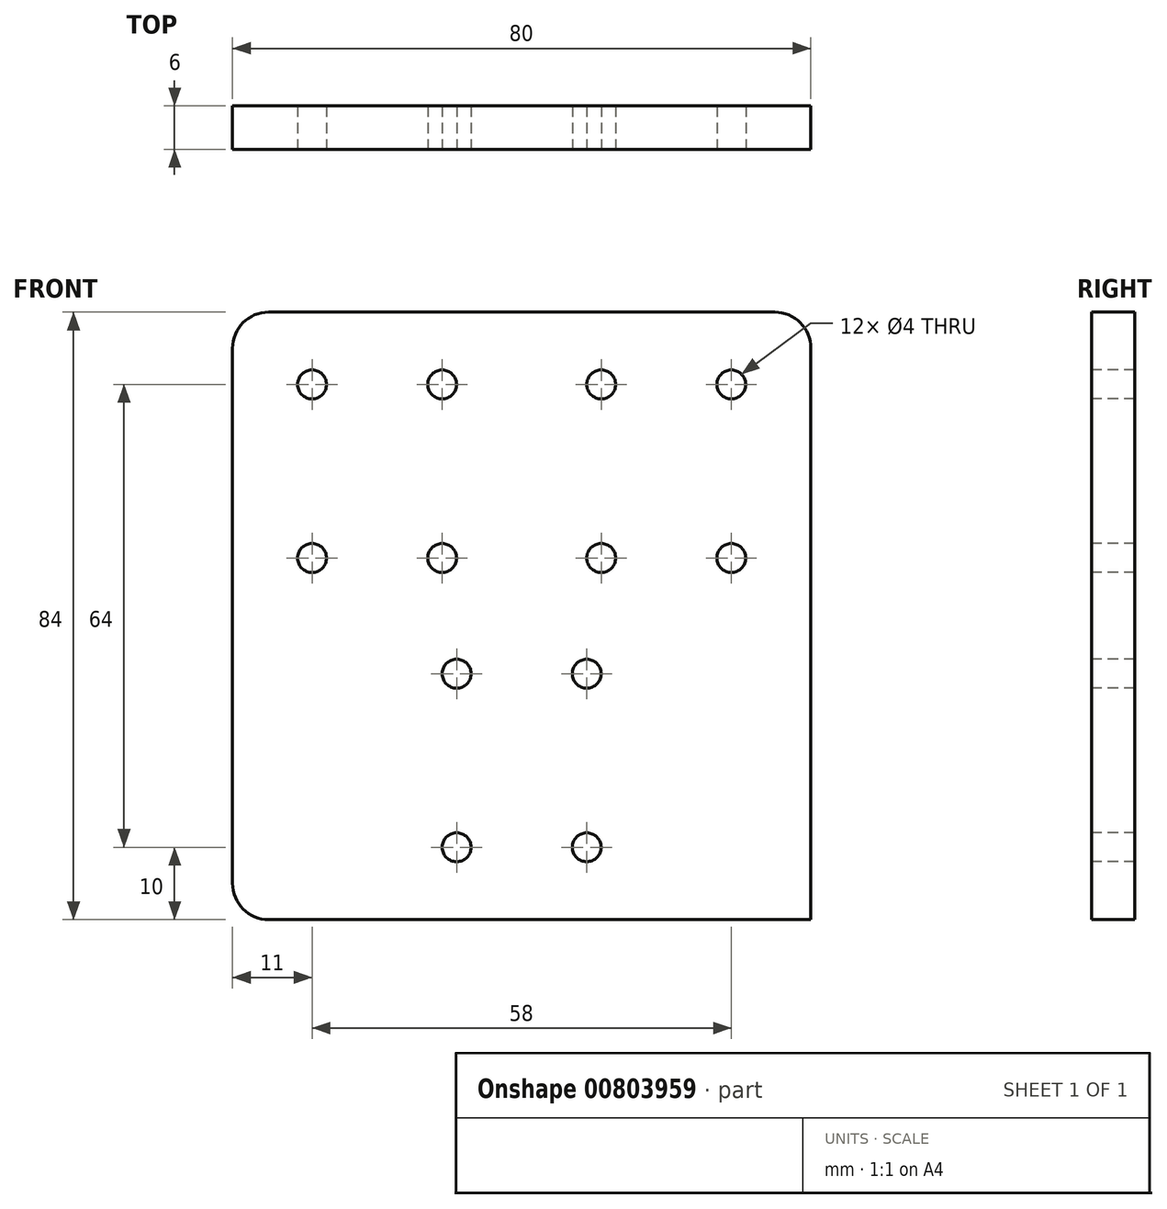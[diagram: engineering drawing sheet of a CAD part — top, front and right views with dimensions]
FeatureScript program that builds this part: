
annotation { "Feature Type Name" : "Feature", "Feature Type Description" : "" }
export const myFeature = defineFeature(function(context is Context, id is Id, definition is map)
    precondition{}
    {
        {
            var Q0;
            Q0=qCreatedBy(makeId("Front.planeOp"),FACE);
            var sketch = newSketch(context, id + "F0", { "sketchPlane" : qUnion([Q0])});
            skLineSegment(sketch, "E0.bottom", {"start": v(40, 42) * mm, "end": v(-40, 42) * mm});
            skLineSegment(sketch, "E0.top", {"start": v(40, -42) * mm, "end": v(-40, -42) * mm});
            skLineSegment(sketch, "E0.left", {"start": v(40, 42) * mm, "end": v(40, -42) * mm});
            skLineSegment(sketch, "E0.right", {"start": v(-40, 42) * mm, "end": v(-40, -42) * mm});
            skPoint(sketch, "E0.middle", {"position": v(0, 0) * mm});
            skLineSegment(sketch, "E1.bottom", {"start": v(5, 37) * mm, "end": v(35, 37) * mm});
            skLineSegment(sketch, "E1.top", {"start": v(5, 3) * mm, "end": v(35, 3) * mm});
            skLineSegment(sketch, "E1.left", {"start": v(5, 37) * mm, "end": v(5, 3) * mm});
            skLineSegment(sketch, "E1.right", {"start": v(35, 37) * mm, "end": v(35, 3) * mm});
            skLineSegment(sketch, "E2.bottom", {"start": v(-35, 37) * mm, "end": v(-5, 37) * mm});
            skLineSegment(sketch, "E2.top", {"start": v(-35, 3) * mm, "end": v(-5, 3) * mm});
            skLineSegment(sketch, "E2.left", {"start": v(-35, 37) * mm, "end": v(-35, 3) * mm});
            skLineSegment(sketch, "E2.right", {"start": v(-5, 37) * mm, "end": v(-5, 3) * mm});
            skLineSegment(sketch, "E3.bottom", {"start": v(-15, -3) * mm, "end": v(15, -3) * mm});
            skLineSegment(sketch, "E3.top", {"start": v(-15, -37) * mm, "end": v(15, -37) * mm});
            skLineSegment(sketch, "E3.left", {"start": v(-15, -3) * mm, "end": v(-15, -37) * mm});
            skLineSegment(sketch, "E3.right", {"start": v(15, -3) * mm, "end": v(15, -37) * mm});
            skPoint(sketch, "E4", {"position": v(0, -20) * mm});
            skLineSegment(sketch, "E5.bottom", {"start": v(9, -8) * mm, "end": v(-9, -8) * mm});
            skLineSegment(sketch, "E5.top", {"start": v(9, -32) * mm, "end": v(-9, -32) * mm});
            skLineSegment(sketch, "E5.left", {"start": v(9, -8) * mm, "end": v(9, -32) * mm});
            skLineSegment(sketch, "E5.right", {"start": v(-9, -8) * mm, "end": v(-9, -32) * mm});
            skPoint(sketch, "E6", {"position": v(20, 20) * mm});
            skPoint(sketch, "E6.positionSnap0", {"position": v(20, 3) * mm});
            skPoint(sketch, "E7", {"position": v(-20, 20) * mm});
            skLineSegment(sketch, "E8.bottom", {"start": v(29, 32) * mm, "end": v(11, 32) * mm});
            skLineSegment(sketch, "E8.top", {"start": v(29, 8) * mm, "end": v(11, 8) * mm});
            skLineSegment(sketch, "E8.left", {"start": v(29, 32) * mm, "end": v(29, 8) * mm});
            skLineSegment(sketch, "E8.right", {"start": v(11, 32) * mm, "end": v(11, 8) * mm});
            skLineSegment(sketch, "E9.bottom", {"start": v(-11, 32) * mm, "end": v(-29, 32) * mm});
            skLineSegment(sketch, "E9.top", {"start": v(-11, 8) * mm, "end": v(-29, 8) * mm});
            skLineSegment(sketch, "E9.left", {"start": v(-11, 32) * mm, "end": v(-11, 8) * mm});
            skLineSegment(sketch, "E9.right", {"start": v(-29, 32) * mm, "end": v(-29, 8) * mm});
            skPoint(sketch, "E10", {"position": v(28.46, 8.28) * mm});
            skPoint(sketch, "E11", {"position": v(28.42, 7.82) * mm});
            skPoint(sketch, "E12", {"position": v(73.92, -8.03) * mm});
            skPoint(sketch, "E13", {"position": v(104.5, -6.57) * mm});
            skPoint(sketch, "E14", {"position": v(11.55, 8.01) * mm});
            skPoint(sketch, "E15", {"position": v(5, 3) * mm});
            skPoint(sketch, "E16", {"position": v(5, 37) * mm});
            skPoint(sketch, "E17", {"position": v(35, 37) * mm});
            skPoint(sketch, "E18", {"position": v(-5, 37) * mm});
            skPoint(sketch, "E19", {"position": v(-35, 37) * mm});
            skPoint(sketch, "E20", {"position": v(-29, 8) * mm});
            skPoint(sketch, "E21", {"position": v(28.8, 32.13) * mm});
            skPoint(sketch, "E22", {"position": v(29, 32) * mm});
            skPoint(sketch, "E23", {"position": v(29, 8) * mm});
            skPoint(sketch, "E24", {"position": v(11, 8) * mm});
            skPoint(sketch, "E25", {"position": v(9, -8) * mm});
            skPoint(sketch, "E26", {"position": v(9, -32) * mm});
            skPoint(sketch, "E27", {"position": v(-9, -32) * mm});
            skPoint(sketch, "E28", {"position": v(-9, -8) * mm});
            skSolve(sketch);
        }
        {
            var Q0;
            Q0=makeQuery(id+"F0.imprint","IMPRINT",FACE,{"disambiguationData":[TD([[makeQuery(id+"F0.imprint","IMPRINT",EDGE,{"derivedFrom":sQuery(id+"F0.wireOp",EDGE,"E9.bottom")}),1.0]])]});
            var Q1;
            Q1=makeQuery(id+"F0.imprint","IMPRINT",FACE,{"disambiguationData":[TD([[makeQuery(id+"F0.imprint","IMPRINT",EDGE,{"derivedFrom":sQuery(id+"F0.wireOp",EDGE,"E2.bottom")}),-1.0]])]});
            var Q2;
            Q2=makeQuery(id+"F0.imprint","IMPRINT",FACE,{"disambiguationData":[TD([[makeQuery(id+"F0.imprint","IMPRINT",EDGE,{"derivedFrom":sQuery(id+"F0.wireOp",EDGE,"E1.bottom")}),-1.0]])]});
            var Q3;
            Q3=makeQuery(id+"F0.imprint","IMPRINT",FACE,{"disambiguationData":[TD([[makeQuery(id+"F0.imprint","IMPRINT",EDGE,{"derivedFrom":sQuery(id+"F0.wireOp",EDGE,"E0.bottom")}),1.0]])]});
            var Q4;
            Q4=makeQuery(id+"F0.imprint","IMPRINT",FACE,{"disambiguationData":[TD([[makeQuery(id+"F0.imprint","IMPRINT",EDGE,{"derivedFrom":sQuery(id+"F0.wireOp",EDGE,"E8.bottom")}),1.0]])]});
            var Q5;
            Q5=makeQuery(id+"F0.imprint","IMPRINT",FACE,{"disambiguationData":[TD([[makeQuery(id+"F0.imprint","IMPRINT",EDGE,{"derivedFrom":sQuery(id+"F0.wireOp",EDGE,"E3.bottom")}),-1.0]])]});
            var Q6;
            Q6=makeQuery(id+"F0.imprint","IMPRINT",FACE,{"disambiguationData":[TD([[makeQuery(id+"F0.imprint","IMPRINT",EDGE,{"derivedFrom":sQuery(id+"F0.wireOp",EDGE,"E5.bottom")}),1.0]])]});
            extrude(context, id + "F1", {"entities" : qUnion([Q0, Q1, Q2, Q3, Q4, Q5, Q6]), "depth" : 6 * mm, "offsetDistance" : 25 * mm});
        }
        {
            var Q0;
            Q0=sQuery(id+"F0.wireOp",VERTEX,"E9.right.start");
            var Q1;
            Q1=sQuery(id+"F0.wireOp",VERTEX,"E9.bottom.start");
            var Q2;
            Q2=sQuery(id+"F0.wireOp",VERTEX,"E9.top.end");
            var Q3;
            Q3=sQuery(id+"F0.wireOp",VERTEX,"E9.left.end");
            var Q4;
            Q4=sQuery(id+"F0.wireOp",VERTEX,"E8.right.start");
            var Q5;
            Q5=sQuery(id+"F0.wireOp",VERTEX,"E22");
            var Q6;
            Q6=sQuery(id+"F0.wireOp",VERTEX,"E8.top.start");
            var Q7;
            Q7=sQuery(id+"F0.wireOp",VERTEX,"E8.top.end");
            var Q8;
            Q8=sQuery(id+"F0.wireOp",VERTEX,"E5.bottom.start");
            var Q9;
            Q9=sQuery(id+"F0.wireOp",VERTEX,"E5.right.start");
            var Q10;
            Q10=sQuery(id+"F0.wireOp",VERTEX,"E5.top.end");
            var Q11;
            Q11=sQuery(id+"F0.wireOp",VERTEX,"E26");
            var Q12;
            Q12=makeQuery(id+"F1.opExtrude","SWEPT_BODY",BODY,{"disambiguationData":[OSD([sQuery(id+"F0.wireOp",EDGE,"E0.bottom"),sQuery(id+"F0.wireOp",EDGE,"E0.top"),sQuery(id+"F0.wireOp",EDGE,"E0.left"),sQuery(id+"F0.wireOp",EDGE,"E0.right")])]});
            hole(context, id + "F2", {"style" : HoleStyle.SIMPLE, "endStyle" : HoleEndStyle.THROUGH, "oppositeDirection" : true, "holeDiameter" : 4 * mm, "majorDiameter" : 5 * mm, "isTappedThrough" : true, "tappedDepth" : 12 * mm, "tapClearance" : 3, "locations" : qUnion([Q0, Q1, Q2, Q3, Q4, Q5, Q6, Q7, Q8, Q9, Q10, Q11]), "scope" : qUnion([Q12])});
        }
        {
            var Q0;
            Q0=makeQuery(id+"F1.opExtrude","SWEPT_EDGE",EDGE,{"disambiguationData":[OSD([sQuery(id+"F0.wireOp",EDGE,"E0.bottom"),sQuery(id+"F0.wireOp",EDGE,"E0.right")])]});
            var Q1;
            Q1=makeQuery(id+"F1.opExtrude","SWEPT_EDGE",EDGE,{"disambiguationData":[OSD([sQuery(id+"F0.wireOp",EDGE,"E0.top"),sQuery(id+"F0.wireOp",EDGE,"E0.right")])]});
            var Q2;
            Q2=makeQuery(id+"F1.opExtrude","SWEPT_EDGE",EDGE,{"disambiguationData":[OSD([sQuery(id+"F0.wireOp",EDGE,"E0.bottom"),sQuery(id+"F0.wireOp",EDGE,"E0.left")])]});
            fillet(context, id + "F3", {"entities" : qUnion([Q0, Q1, Q2]), "radius" : 5 * mm, "tangentPropagation" : true, "allowEdgeOverflow" : false});
        }
    });
